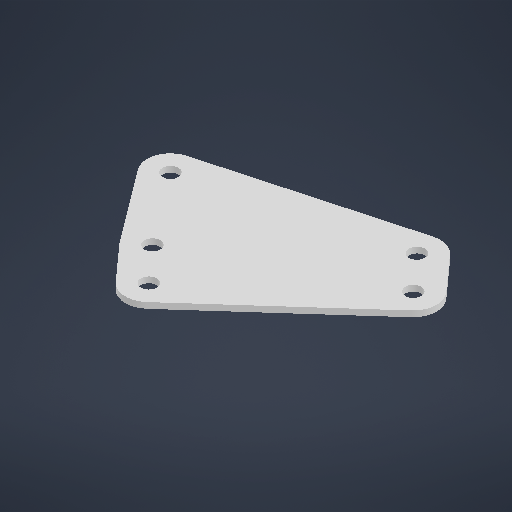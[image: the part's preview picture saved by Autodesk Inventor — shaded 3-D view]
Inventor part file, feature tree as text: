
AUTODESK INVENTOR PART (.ipt)
format: ipt  version: 2025.2 (Build 292293000, 293)  size: 221,184 bytes
history: native  units: in
note: dims shown in document units (in); Inventor stores cm internally (conversion verified against a paired STEP export)
features: extrude x1, sketch x1
ambient origin geometry x8: Origin, YZ Plane, XZ Plane, XY Plane, X Axis, Y Axis, Z Axis, Center Point
bodies: Solid1 (feature_tree)
feature tree (2):
  extrude  "Extrusion1"  Depth=0.0625in
  sketch  "Sketch1"  dims[d0=0.172in d1=0.172in d2=0.172in d3=0.5in d4=0.5in d5=0.5in d6=0.0625in d7=0.0in]
